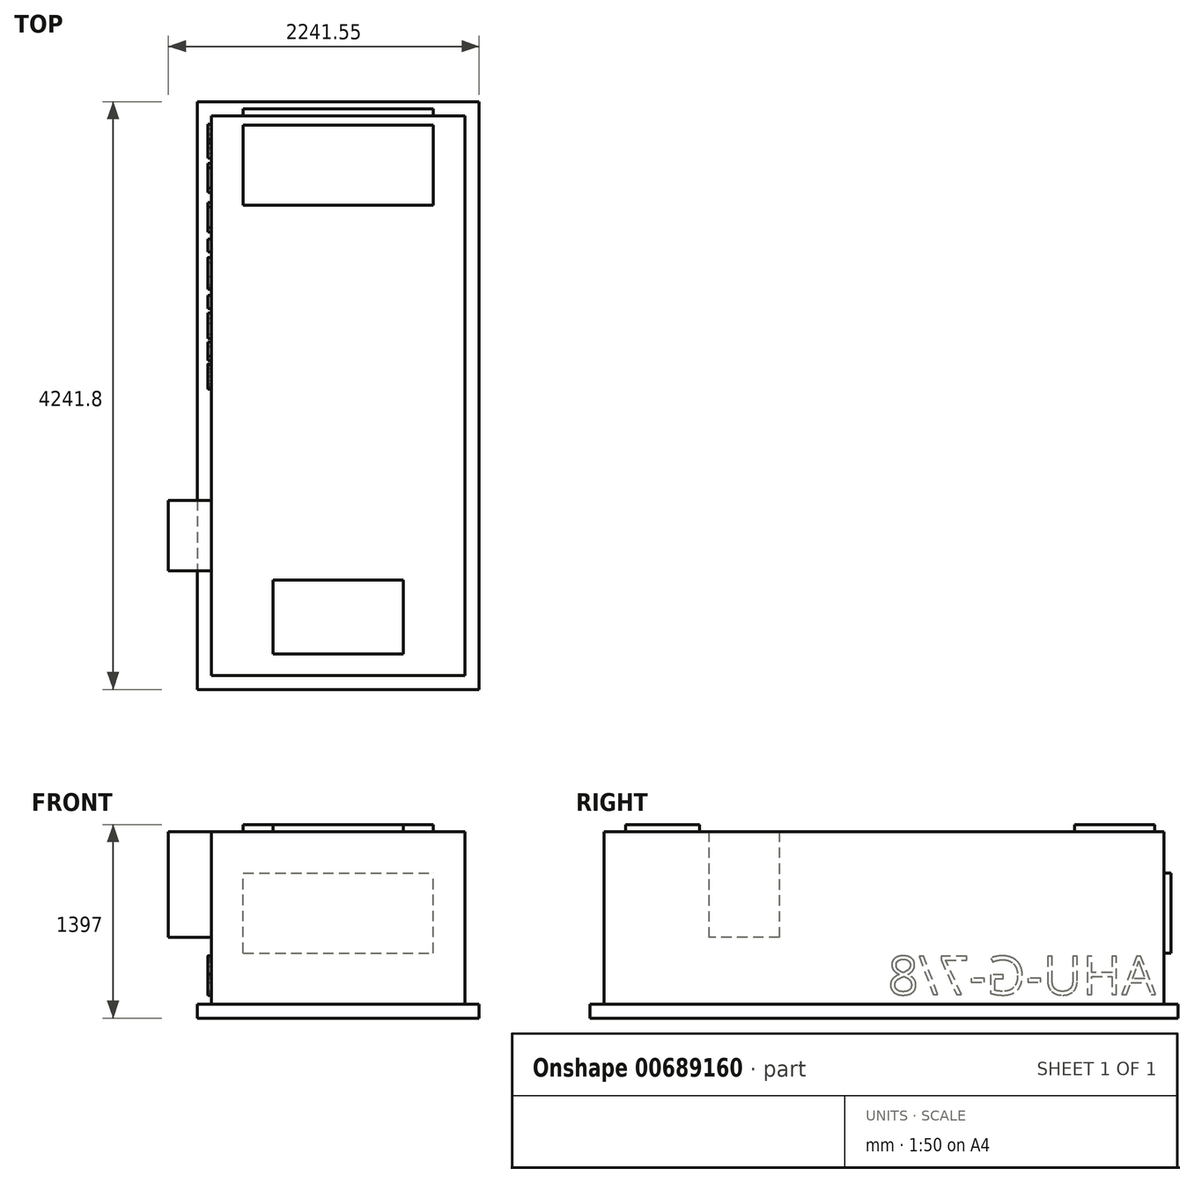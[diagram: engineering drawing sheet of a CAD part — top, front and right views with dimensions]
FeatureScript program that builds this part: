
annotation { "Feature Type Name" : "Feature", "Feature Type Description" : "" }
export const myFeature = defineFeature(function(context is Context, id is Id, definition is map)
    precondition{}
    {
        {
            var Q0;
            Q0=qCreatedBy(makeId("Front.planeOp"),FACE);
            var sketch = newSketch(context, id + "F0", { "sketchPlane" : qUnion([Q0])});
            skLineSegment(sketch, "E0.bottom", {"start": v(-639.94, 692.16) * mm, "end": v(1188.86, 692.16) * mm});
            skLineSegment(sketch, "E0.top", {"start": v(-639.94, -552.44) * mm, "end": v(1188.86, -552.44) * mm});
            skLineSegment(sketch, "E0.left", {"start": v(-639.94, 692.16) * mm, "end": v(-639.94, -552.44) * mm});
            skLineSegment(sketch, "E0.right", {"start": v(1188.86, 692.16) * mm, "end": v(1188.86, -552.44) * mm});
            skSolve(sketch);
        }
        {
            var Q0;
            Q0=qSketchRegion(id+"F0",true);
            extrude(context, id + "F1", {"entities" : qUnion([Q0]), "depth" : 4038.6 * mm, "offsetDistance" : 25.4 * mm});
        }
        {
            var Q0;
            Q0=makeQuery(id+"F1.opExtrude","SWEPT_FACE",FACE,{"disambiguationData":[OSD([sQuery(id+"F0.wireOp",EDGE,"E0.bottom")])]});
            var sketch = newSketch(context, id + "F2", { "sketchPlane" : qUnion([Q0])});
            skLineSegment(sketch, "E1.bottom", {"start": v(-195.44, -3349.63) * mm, "end": v(744.36, -3349.63) * mm});
            skLineSegment(sketch, "E1.top", {"start": v(-195.44, -3883.03) * mm, "end": v(744.36, -3883.03) * mm});
            skLineSegment(sketch, "E1.left", {"start": v(-195.44, -3349.63) * mm, "end": v(-195.44, -3883.03) * mm});
            skLineSegment(sketch, "E1.right", {"start": v(744.36, -3349.63) * mm, "end": v(744.36, -3883.03) * mm});
            skSolve(sketch);
        }
        {
            var Q0;
            Q0 = qSketchRegion(id + "F2", true);
            extrude(context, id + "F3", {"entities" : qUnion([Q0]), "operationType" : NewBodyOperationType.ADD, "depth" : 50.8 * mm, "offsetDistance" : 25.4 * mm});
        }
        {
            var Q0;
            Q0=makeQuery(id+"F1.opExtrude","CAP_FACE",FACE,{"disambiguationData":[OSD([sQuery(id+"F0.wireOp",EDGE,"E0.bottom"),sQuery(id+"F0.wireOp",EDGE,"E0.top"),sQuery(id+"F0.wireOp",EDGE,"E0.left"),sQuery(id+"F0.wireOp",EDGE,"E0.right")])],"isStart":false});
            var sketch = newSketch(context, id + "F4", { "sketchPlane" : qUnion([Q0])});
            skLineSegment(sketch, "E2.bottom", {"start": v(-741.54, -552.44) * mm, "end": v(1290.46, -552.44) * mm});
            skLineSegment(sketch, "E2.top", {"start": v(-741.54, -654.04) * mm, "end": v(1290.46, -654.04) * mm});
            skLineSegment(sketch, "E2.left", {"start": v(-741.54, -552.44) * mm, "end": v(-741.54, -654.04) * mm});
            skLineSegment(sketch, "E2.right", {"start": v(1290.46, -552.44) * mm, "end": v(1290.46, -654.04) * mm});
            skSolve(sketch);
        }
        {
            var Q0;
            Q0 = qSketchRegion(id + "F4", true);
            extrude(context, id + "F5", {"entities" : qUnion([Q0]), "oppositeDirection" : true, "depth" : 4140.2 * mm, "offsetDistance" : 25.4 * mm});
        }
        {
            var Q0;
            Q0=makeQuery(id+"F5.opExtrude","CAP_FACE",FACE,{"disambiguationData":[OSD([sQuery(id+"F4.wireOp",EDGE,"E2.bottom"),sQuery(id+"F4.wireOp",EDGE,"E2.top"),sQuery(id+"F4.wireOp",EDGE,"E2.left"),sQuery(id+"F4.wireOp",EDGE,"E2.right")])],"isStart":true});
            extrude(context, id + "F6", {"entities" : qUnion([Q0]), "operationType" : NewBodyOperationType.ADD, "depth" : 101.6 * mm, "offsetDistance" : 25.4 * mm});
        }
        {
            var Q0;
            Q0=makeQuery(id+"F1.opExtrude","SWEPT_FACE",FACE,{"disambiguationData":[OSD([sQuery(id+"F0.wireOp",EDGE,"E0.left")])]});
            var sketch = newSketch(context, id + "F7", { "sketchPlane" : qUnion([Q0])});
            skLineSegment(sketch, "E3.bottom", {"start": v(2774.95, 692.16) * mm, "end": v(3282.95, 692.16) * mm});
            skLineSegment(sketch, "E3.top", {"start": v(2774.95, -69.84) * mm, "end": v(3282.95, -69.84) * mm});
            skLineSegment(sketch, "E3.left", {"start": v(2774.95, 692.16) * mm, "end": v(2774.95, -69.84) * mm});
            skLineSegment(sketch, "E3.right", {"start": v(3282.95, 692.16) * mm, "end": v(3282.95, -69.84) * mm});
            skSolve(sketch);
        }
        {
            var Q0;
            Q0 = qSketchRegion(id + "F7", true);
            extrude(context, id + "F8", {"entities" : qUnion([Q0]), "depth" : 311.15 * mm, "offsetDistance" : 25.4 * mm});
        }
        {
            var Q0;
            Q0=makeQuery(id+"F1.opExtrude","SWEPT_FACE",FACE,{"disambiguationData":[OSD([sQuery(id+"F0.wireOp",EDGE,"E0.left")])]});
            var sketch = newSketch(context, id + "F9", { "sketchPlane" : qUnion([Q0])});
            skText(sketch, "E4", { "text": "AHU-G-7/8", "fontName": "OpenSans-Regular.ttf"});
            const initialGuessF9  = {"E4": [0.06038, -0.48503, 1, 0, 0.2794]};
            skSetInitialGuess(sketch, initialGuessF9);
            skSolve(sketch);
        }
        {
            var Q0;
            Q0 = qSketchRegion(id + "F9", true);
            extrude(context, id + "F10", {"entities" : qUnion([Q0]), "operationType" : NewBodyOperationType.ADD, "depth" : 25.4 * mm, "offsetDistance" : 25.4 * mm});
        }
        {
            var Q0;
            Q0=makeQuery(id+"F1.opExtrude","SWEPT_FACE",FACE,{"disambiguationData":[OSD([sQuery(id+"F0.wireOp",EDGE,"E0.bottom")])]});
            var sketch = newSketch(context, id + "F11", { "sketchPlane" : qUnion([Q0])});
            skLineSegment(sketch, "E5.bottom", {"start": v(-411.34, -66.68) * mm, "end": v(960.26, -66.67) * mm});
            skLineSegment(sketch, "E5.top", {"start": v(-411.34, -644.53) * mm, "end": v(960.26, -644.52) * mm});
            skLineSegment(sketch, "E5.left", {"start": v(-411.34, -66.68) * mm, "end": v(-411.34, -644.53) * mm});
            skLineSegment(sketch, "E5.right", {"start": v(960.26, -66.67) * mm, "end": v(960.26, -644.52) * mm});
            skSolve(sketch);
        }
        {
            var Q0;
            Q0 = qSketchRegion(id + "F11", true);
            extrude(context, id + "F12", {"entities" : qUnion([Q0]), "operationType" : NewBodyOperationType.ADD, "depth" : 50.8 * mm, "offsetDistance" : 25.4 * mm});
        }
        {
            var Q0;
            Q0=makeQuery(id+"F1.opExtrude","CAP_FACE",FACE,{"disambiguationData":[OSD([sQuery(id+"F0.wireOp",EDGE,"E0.bottom"),sQuery(id+"F0.wireOp",EDGE,"E0.top"),sQuery(id+"F0.wireOp",EDGE,"E0.left"),sQuery(id+"F0.wireOp",EDGE,"E0.right")])],"isStart":true});
            var sketch = newSketch(context, id + "F13", { "sketchPlane" : qUnion([Q0])});
            skLineSegment(sketch, "E6.bottom", {"start": v(411.34, -184.14) * mm, "end": v(-960.26, -184.14) * mm});
            skLineSegment(sketch, "E6.top", {"start": v(411.34, 393.71) * mm, "end": v(-960.26, 393.71) * mm});
            skLineSegment(sketch, "E6.left", {"start": v(411.34, -184.14) * mm, "end": v(411.34, 393.71) * mm});
            skLineSegment(sketch, "E6.right", {"start": v(-960.26, -184.14) * mm, "end": v(-960.26, 393.71) * mm});
            skSolve(sketch);
        }
        {
            var Q0;
            Q0 = qSketchRegion(id + "F13", true);
            extrude(context, id + "F14", {"entities" : qUnion([Q0]), "operationType" : NewBodyOperationType.ADD, "depth" : 50.8 * mm, "offsetDistance" : 25.4 * mm});
        }
    });
